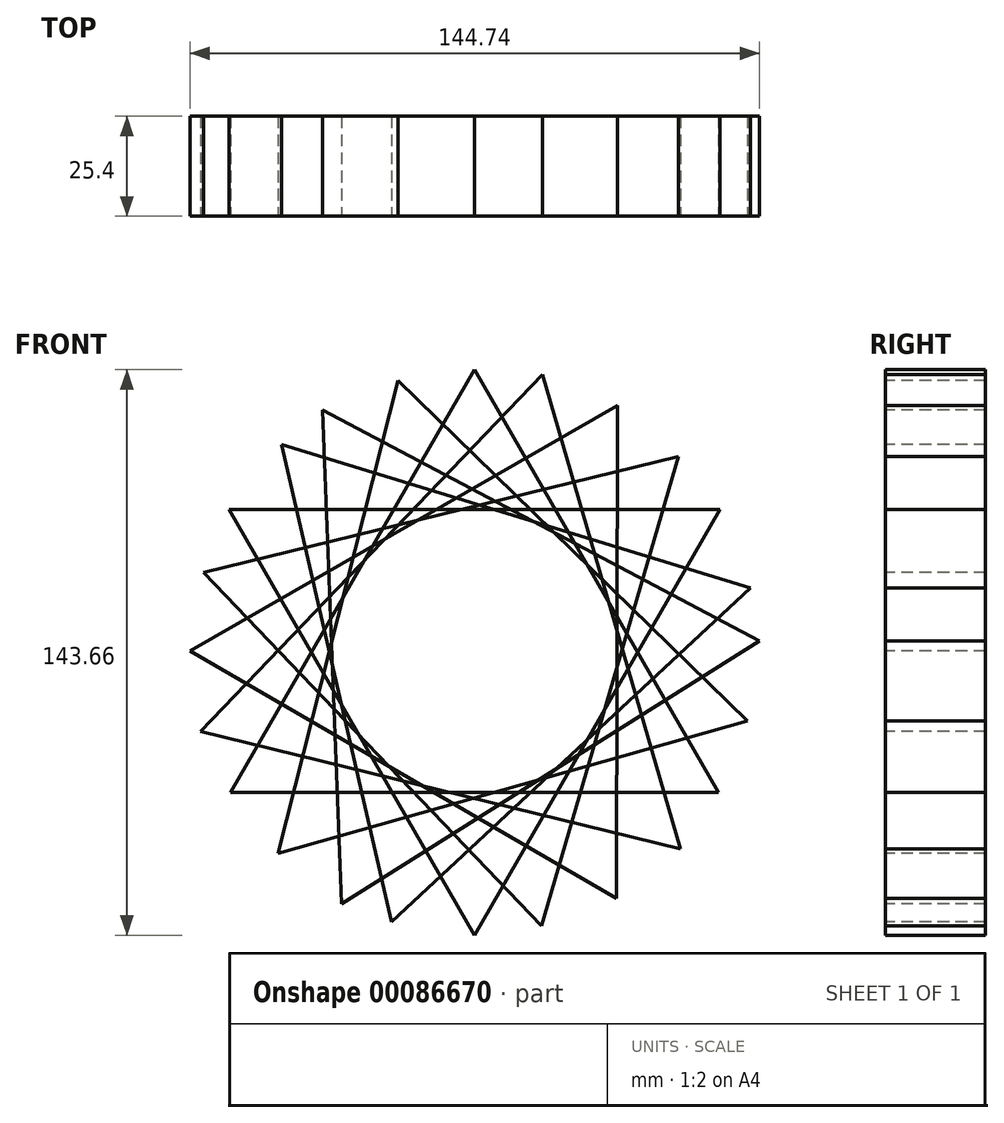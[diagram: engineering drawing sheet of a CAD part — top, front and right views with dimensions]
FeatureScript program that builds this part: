
annotation { "Feature Type Name" : "Feature", "Feature Type Description" : "" }
export const myFeature = defineFeature(function(context is Context, id is Id, definition is map)
    precondition{}
    {
        {
            var Q0;
            Q0=qCreatedBy(makeId("Front.planeOp"),FACE);
            var sketch = newSketch(context, id + "F0", { "sketchPlane" : qUnion([Q0])});
            skCircle(sketch, "E0", {"center": v(0, 0) * mm, "radius": 72.35 * mm});
            skCircle(sketch, "E1", {"center": v(0, 0) * mm, "radius": 77.75 * mm});
            skSolve(sketch);
        }
        {
            var Q0;
            Q0=makeQuery(id+"F0.imprint","IMPRINT",FACE,{"disambiguationData":[TD([[makeQuery(id+"F0.imprint","IMPRINT",EDGE,{"derivedFrom":sQuery(id+"F0.wireOp",EDGE,"E0")}),1.0]])]});
            var sketch = newSketch(context, id + "F1", { "sketchPlane" : qUnion([Q0])});
            skCircle(sketch, "E2.cCircle", {"center": v(0, 0) * mm, "radius": 72.3 * mm, "construction": true});
            skLineSegment(sketch, "E2.0", {"start": v(36.26, 62.56) * mm, "end": v(36.05, -62.68) * mm});
            skLineSegment(sketch, "E2.1", {"start": v(36.05, -62.68) * mm, "end": v(-72.3, 0.12) * mm});
            skLineSegment(sketch, "E2.2", {"start": v(-72.3, 0.12) * mm, "end": v(36.26, 62.56) * mm});
            skSolve(sketch);
        }
        {
            var Q0;
            Q0=sQuery(id+"F1.wireOp",EDGE,"E2.0");
            var Q1;
            Q1=sQuery(id+"F1.wireOp",EDGE,"E2.2");
            var Q2;
            Q2=sQuery(id+"F1.wireOp",EDGE,"E2.1");
            extrude(context, id + "F2", {"bodyType" : ToolBodyType.SURFACE, "surfaceEntities" : qUnion([Q0, Q1, Q2]), "depth" : 25.4 * mm});
        }
        {
            var Q0;
            Q0=makeQuery(id+"F0.imprint","IMPRINT",FACE,{"disambiguationData":[TD([[makeQuery(id+"F0.imprint","IMPRINT",EDGE,{"derivedFrom":sQuery(id+"F0.wireOp",EDGE,"E0")}),1.0]])]});
            var sketch = newSketch(context, id + "F3", { "sketchPlane" : qUnion([Q0])});
            skCircle(sketch, "E3.cCircle", {"center": v(0, 0) * mm, "radius": 72.07 * mm, "construction": true});
            skLineSegment(sketch, "E3.0", {"start": v(0, -72.07) * mm, "end": v(-62.42, 36.04) * mm});
            skLineSegment(sketch, "E3.1", {"start": v(-62.42, 36.04) * mm, "end": v(62.42, 36.04) * mm});
            skLineSegment(sketch, "E3.2", {"start": v(62.42, 36.04) * mm, "end": v(0, -72.07) * mm});
            skSolve(sketch);
        }
        {
            var Q0;
            Q0=sQuery(id+"F3.wireOp",EDGE,"E3.2");
            var Q1;
            Q1=sQuery(id+"F3.wireOp",EDGE,"E3.1");
            var Q2;
            Q2=sQuery(id+"F3.wireOp",EDGE,"E3.0");
            extrude(context, id + "F4", {"bodyType" : ToolBodyType.SURFACE, "surfaceEntities" : qUnion([Q0, Q1, Q2]), "depth" : 25.4 * mm});
        }
        {
            var Q0;
            Q0=makeQuery(id+"F0.imprint","IMPRINT",FACE,{"disambiguationData":[TD([[makeQuery(id+"F0.imprint","IMPRINT",EDGE,{"derivedFrom":sQuery(id+"F0.wireOp",EDGE,"E0")}),1.0]])]});
            var sketch = newSketch(context, id + "F5", { "sketchPlane" : qUnion([Q0])});
            skCircle(sketch, "E4.cCircle", {"center": v(0, 0) * mm, "radius": 71.51 * mm, "construction": true});
            skLineSegment(sketch, "E4.0", {"start": v(69.32, -17.57) * mm, "end": v(-49.88, -51.25) * mm});
            skLineSegment(sketch, "E4.1", {"start": v(-49.88, -51.25) * mm, "end": v(-19.45, 68.82) * mm});
            skLineSegment(sketch, "E4.2", {"start": v(-19.45, 68.82) * mm, "end": v(69.32, -17.57) * mm});
            skSolve(sketch);
        }
        {
            var Q0;
            Q0=sQuery(id+"F5.wireOp",EDGE,"E4.2");
            var Q1;
            Q1=sQuery(id+"F5.wireOp",EDGE,"E4.1");
            var Q2;
            Q2=sQuery(id+"F5.wireOp",EDGE,"E4.0");
            extrude(context, id + "F6", {"bodyType" : ToolBodyType.SURFACE, "surfaceEntities" : qUnion([Q0, Q1, Q2]), "depth" : 25.4 * mm});
        }
        {
            var Q0;
            Q0=makeQuery(id+"F0.imprint","IMPRINT",FACE,{"disambiguationData":[TD([[makeQuery(id+"F0.imprint","IMPRINT",EDGE,{"derivedFrom":sQuery(id+"F0.wireOp",EDGE,"E0")}),1.0]])]});
            var sketch = newSketch(context, id + "F7", { "sketchPlane" : qUnion([Q0])});
            skCircle(sketch, "E5.cCircle", {"center": v(0, 0) * mm, "radius": 71.87 * mm, "construction": true});
            skLineSegment(sketch, "E5.0", {"start": v(70.04, 16.14) * mm, "end": v(-21.05, -68.72) * mm});
            skLineSegment(sketch, "E5.1", {"start": v(-21.05, -68.72) * mm, "end": v(-49, 52.59) * mm});
            skLineSegment(sketch, "E5.2", {"start": v(-49, 52.59) * mm, "end": v(70.04, 16.14) * mm});
            skSolve(sketch);
        }
        {
            var Q0;
            Q0=sQuery(id+"F7.wireOp",EDGE,"E5.2");
            var Q1;
            Q1=sQuery(id+"F7.wireOp",EDGE,"E5.0");
            var Q2;
            Q2=sQuery(id+"F7.wireOp",EDGE,"E5.1");
            extrude(context, id + "F8", {"bodyType" : ToolBodyType.SURFACE, "surfaceEntities" : qUnion([Q0, Q1, Q2]), "depth" : 25.4 * mm});
        }
        {
            var Q0;
            Q0=makeQuery(id+"F0.imprint","IMPRINT",FACE,{"disambiguationData":[TD([[makeQuery(id+"F0.imprint","IMPRINT",EDGE,{"derivedFrom":sQuery(id+"F0.wireOp",EDGE,"E0")}),1.0]])]});
            var sketch = newSketch(context, id + "F9", { "sketchPlane" : qUnion([Q0])});
            skCircle(sketch, "E6.cCircle", {"center": v(0, 0) * mm, "radius": 71.77 * mm, "construction": true});
            skLineSegment(sketch, "E6.0", {"start": v(51.87, 49.6) * mm, "end": v(17.02, -69.72) * mm});
            skLineSegment(sketch, "E6.1", {"start": v(17.02, -69.72) * mm, "end": v(-68.9, 20.12) * mm});
            skLineSegment(sketch, "E6.2", {"start": v(-68.9, 20.12) * mm, "end": v(51.87, 49.6) * mm});
            skSolve(sketch);
        }
        {
            var Q0;
            Q0=sQuery(id+"F9.wireOp",EDGE,"E6.0");
            var Q1;
            Q1=sQuery(id+"F9.wireOp",EDGE,"E6.2");
            var Q2;
            Q2=sQuery(id+"F9.wireOp",EDGE,"E6.1");
            extrude(context, id + "F10", {"bodyType" : ToolBodyType.SURFACE, "surfaceEntities" : qUnion([Q0, Q1, Q2]), "depth" : 25.4 * mm});
        }
        {
            var Q0;
            Q0=makeQuery(id+"F0.imprint","IMPRINT",FACE,{"disambiguationData":[TD([[makeQuery(id+"F0.imprint","IMPRINT",EDGE,{"derivedFrom":sQuery(id+"F0.wireOp",EDGE,"E0")}),1.0]])]});
            var sketch = newSketch(context, id + "F11", { "sketchPlane" : qUnion([Q0])});
            skCircle(sketch, "E7.cCircle", {"center": v(0, 0) * mm, "radius": 72.47 * mm, "construction": true});
            skLineSegment(sketch, "E7.0", {"start": v(17.21, 70.4) * mm, "end": v(52.36, -50.1) * mm});
            skLineSegment(sketch, "E7.1", {"start": v(52.36, -50.1) * mm, "end": v(-69.57, -20.3) * mm});
            skLineSegment(sketch, "E7.2", {"start": v(-69.57, -20.3) * mm, "end": v(17.21, 70.4) * mm});
            skSolve(sketch);
        }
        {
            var Q0;
            Q0=sQuery(id+"F11.wireOp",EDGE,"E7.0");
            var Q1;
            Q1=sQuery(id+"F11.wireOp",EDGE,"E7.2");
            var Q2;
            Q2=sQuery(id+"F11.wireOp",EDGE,"E7.1");
            extrude(context, id + "F12", {"bodyType" : ToolBodyType.SURFACE, "surfaceEntities" : qUnion([Q0, Q1, Q2]), "depth" : 25.4 * mm});
        }
        {
            var Q0;
            Q0=makeQuery(id+"F0.imprint","IMPRINT",FACE,{"disambiguationData":[TD([[makeQuery(id+"F0.imprint","IMPRINT",EDGE,{"derivedFrom":sQuery(id+"F0.wireOp",EDGE,"E0")}),1.0]])]});
            var sketch = newSketch(context, id + "F13", { "sketchPlane" : qUnion([Q0])});
            skCircle(sketch, "E8.cCircle", {"center": v(0, 0) * mm, "radius": 71.6 * mm, "construction": true});
            skLineSegment(sketch, "E8.0", {"start": v(0, 71.6) * mm, "end": v(62, -35.8) * mm});
            skLineSegment(sketch, "E8.1", {"start": v(62, -35.8) * mm, "end": v(-62, -35.8) * mm});
            skLineSegment(sketch, "E8.2", {"start": v(-62, -35.8) * mm, "end": v(0, 71.6) * mm});
            skSolve(sketch);
        }
        {
            var Q0;
            Q0=sQuery(id+"F13.wireOp",EDGE,"E8.0");
            var Q1;
            Q1=sQuery(id+"F13.wireOp",EDGE,"E8.2");
            var Q2;
            Q2=sQuery(id+"F13.wireOp",EDGE,"E8.1");
            extrude(context, id + "F14", {"bodyType" : ToolBodyType.SURFACE, "surfaceEntities" : qUnion([Q0, Q1, Q2]), "depth" : 25.4 * mm});
        }
        {
            var Q0;
            Q0=makeQuery(id+"F0.imprint","IMPRINT",FACE,{"disambiguationData":[TD([[makeQuery(id+"F0.imprint","IMPRINT",EDGE,{"derivedFrom":sQuery(id+"F0.wireOp",EDGE,"E0")}),1.0]])]});
            var sketch = newSketch(context, id + "F15", { "sketchPlane" : qUnion([Q0])});
            skCircle(sketch, "E9.cCircle", {"center": v(0, 0) * mm, "radius": 72.48 * mm, "construction": true});
            skLineSegment(sketch, "E9.0", {"start": v(72.43, 2.75) * mm, "end": v(-33.83, -64.1) * mm});
            skLineSegment(sketch, "E9.1", {"start": v(-33.83, -64.1) * mm, "end": v(-38.6, 61.35) * mm});
            skLineSegment(sketch, "E9.2", {"start": v(-38.6, 61.35) * mm, "end": v(72.43, 2.75) * mm});
            skSolve(sketch);
        }
        {
            var Q0;
            Q0=sQuery(id+"F15.wireOp",EDGE,"E9.2");
            var Q1;
            Q1=sQuery(id+"F15.wireOp",EDGE,"E9.1");
            var Q2;
            Q2=sQuery(id+"F15.wireOp",EDGE,"E9.0");
            extrude(context, id + "F16", {"bodyType" : ToolBodyType.SURFACE, "surfaceEntities" : qUnion([Q0, Q1, Q2]), "depth" : 25.4 * mm});
        }
    });
